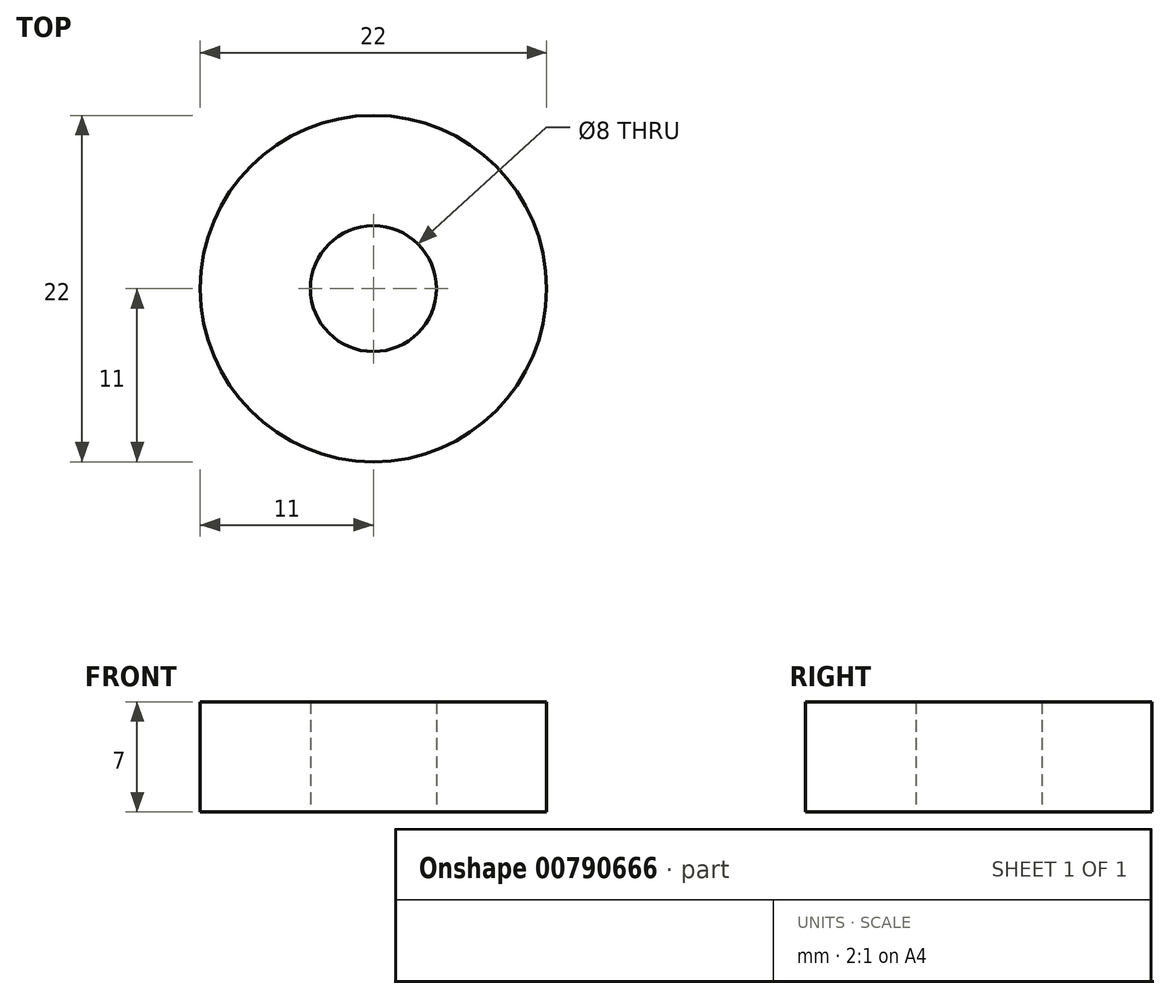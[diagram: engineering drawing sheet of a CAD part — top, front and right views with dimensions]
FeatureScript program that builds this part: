
annotation { "Feature Type Name" : "Feature", "Feature Type Description" : "" }
export const myFeature = defineFeature(function(context is Context, id is Id, definition is map)
    precondition{}
    {
        {
            var Q0;
            Q0=qCreatedBy(makeId("Top.planeOp"),FACE);
            var sketch = newSketch(context, id + "F0", { "sketchPlane" : qUnion([Q0])});
            skCircle(sketch, "E0", {"center": v(0, 0) * mm, "radius": 11 * mm});
            skCircle(sketch, "E1", {"center": v(0, 0) * mm, "radius": 4 * mm});
            skSolve(sketch);
        }
        {
            var Q0;
            Q0 = qSketchRegion(id + "F0", true);
            extrude(context, id + "F1", {"entities" : qUnion([Q0]), "depth" : 7 * mm, "offsetDistance" : 25 * mm});
        }
    });
